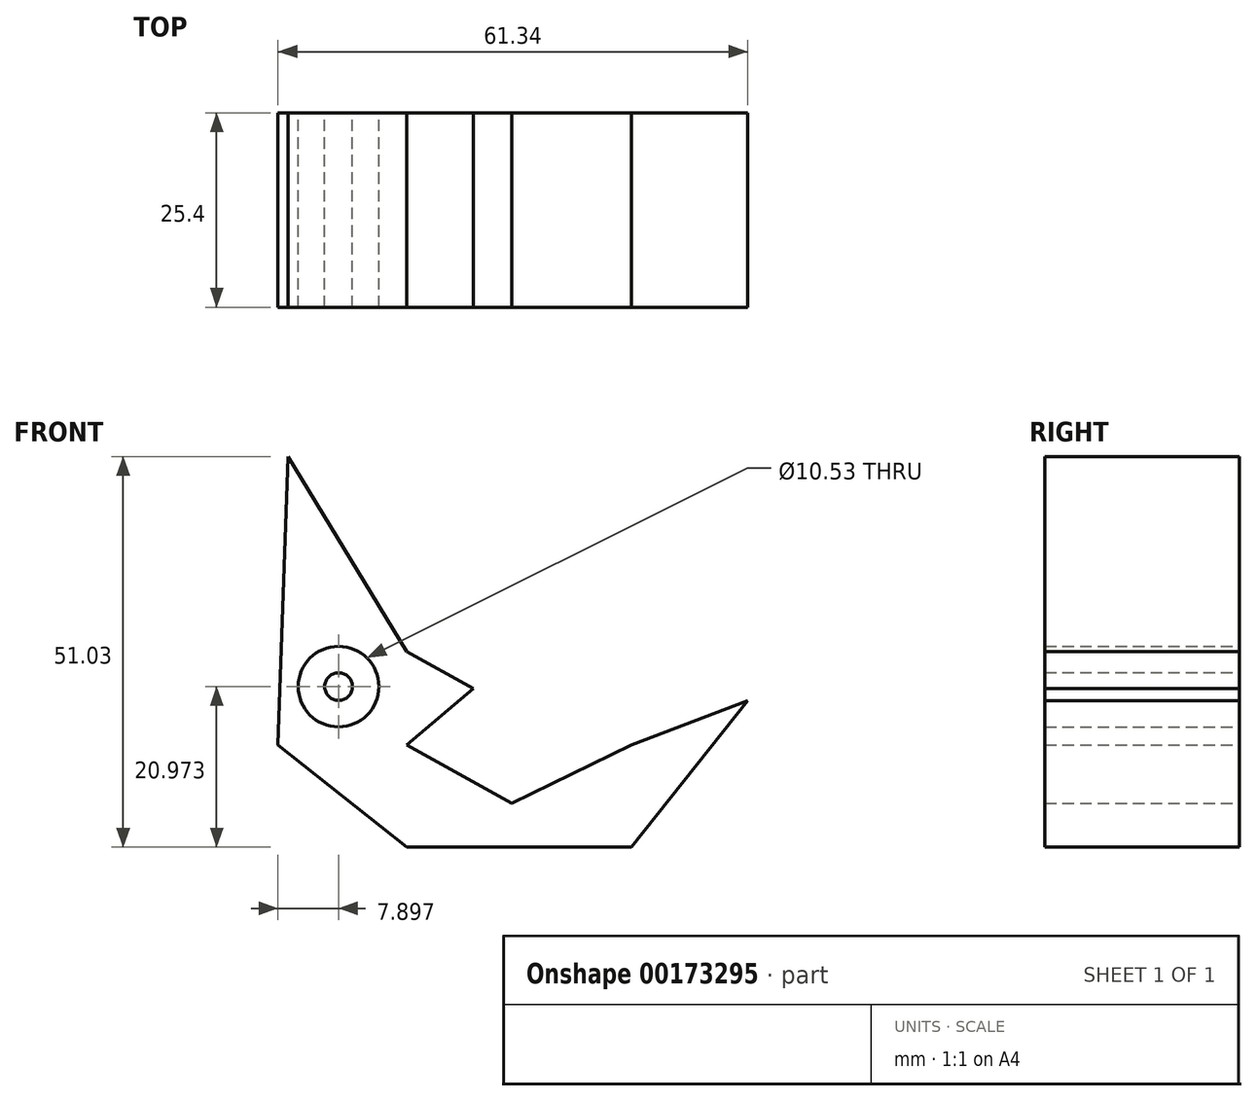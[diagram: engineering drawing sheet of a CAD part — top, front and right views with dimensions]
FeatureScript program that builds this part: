
annotation { "Feature Type Name" : "Feature", "Feature Type Description" : "" }
export const myFeature = defineFeature(function(context is Context, id is Id, definition is map)
    precondition{}
    {
        {
            var Q0;
            Q0=qCreatedBy(makeId("Front.planeOp"),FACE);
            var sketch = newSketch(context, id + "F0", { "sketchPlane" : qUnion([Q0])});
            skLineSegment(sketch, "E0.top", {"start": v(-31.59, 4.51) * mm, "end": v(-2.26, 4.51) * mm});
            skLineSegment(sketch, "E1", {"start": v(-31.59, 17.88) * mm, "end": v(-17.88, 10.24) * mm});
            skLineSegment(sketch, "E2", {"start": v(-2.26, 17.88) * mm, "end": v(-17.88, 10.24) * mm});
            skLineSegment(sketch, "E3", {"start": v(-31.59, 4.51) * mm, "end": v(-48.41, 17.88) * mm});
            skLineSegment(sketch, "E4", {"start": v(-48.41, 17.88) * mm, "end": v(-47.1, 55.54) * mm});
            skLineSegment(sketch, "E5", {"start": v(-31.59, 17.88) * mm, "end": v(-22.9, 25.2) * mm});
            skLineSegment(sketch, "E6", {"start": v(-22.9, 25.2) * mm, "end": v(-31.59, 30.05) * mm});
            skLineSegment(sketch, "E7", {"start": v(-31.59, 30.05) * mm, "end": v(-47.1, 55.54) * mm});
            skLineSegment(sketch, "E8", {"start": v(-2.26, 4.51) * mm, "end": v(12.93, 23.63) * mm});
            skLineSegment(sketch, "E9", {"start": v(12.93, 23.63) * mm, "end": v(-2.26, 17.88) * mm});
            skCircle(sketch, "E10", {"center": v(-40.51, 25.48) * mm, "radius": 5.26 * mm});
            skLineSegment(sketch, "E11", {"start": v(-19.51, 11.15) * mm, "end": v(-17.2, 14.06) * mm});
            skPoint(sketch, "E11.endSnap0", {"position": v(-10.07, 14.06) * mm});
            skLineSegment(sketch, "E12", {"start": v(-17.2, 14.06) * mm, "end": v(-13.87, 12.2) * mm});
            skLineSegment(sketch, "E13", {"start": v(-13.87, 12.2) * mm, "end": v(-17.2, 14.06) * mm});
            skLineSegment(sketch, "E14", {"start": v(-17.2, 14.06) * mm, "end": v(-13.87, 16.1) * mm});
            skLineSegment(sketch, "E15", {"start": v(-13.87, 16.1) * mm, "end": v(-10.07, 14.06) * mm});
            skLineSegment(sketch, "E16", {"start": v(-13.87, 16.1) * mm, "end": v(-9.15, 17.88) * mm});
            skLineSegment(sketch, "E17", {"start": v(-9.15, 17.88) * mm, "end": v(-6.53, 15.79) * mm});
            skLineSegment(sketch, "E18", {"start": v(-9.15, 17.88) * mm, "end": v(-4.07, 20.36) * mm});
            skLineSegment(sketch, "E19", {"start": v(-2.26, 17.88) * mm, "end": v(-4.07, 20.36) * mm});
            skCircle(sketch, "E20", {"center": v(-40.51, 25.48) * mm, "radius": 1.81 * mm});
            skSolve(sketch);
        }
        {
            var Q0;
            Q0=makeQuery(id+"F0.imprint","IMPRINT",FACE,{"disambiguationData":[TD([[makeQuery(id+"F0.imprint","IMPRINT",EDGE,{"derivedFrom":sQuery(id+"F0.wireOp",EDGE,"E0.top")}),1.0]])]});
            var Q1;
            Q1=makeQuery(id+"F0.imprint","IMPRINT",FACE,{"disambiguationData":[TD([[makeQuery(id+"F0.imprint","IMPRINT",EDGE,{"derivedFrom":sQuery(id+"F0.wireOp",EDGE,"E20")}),1.0]])]});
            extrude(context, id + "F1", {"entities" : qUnion([Q0, Q1]), "depth" : 25.4 * mm});
        }
    });
